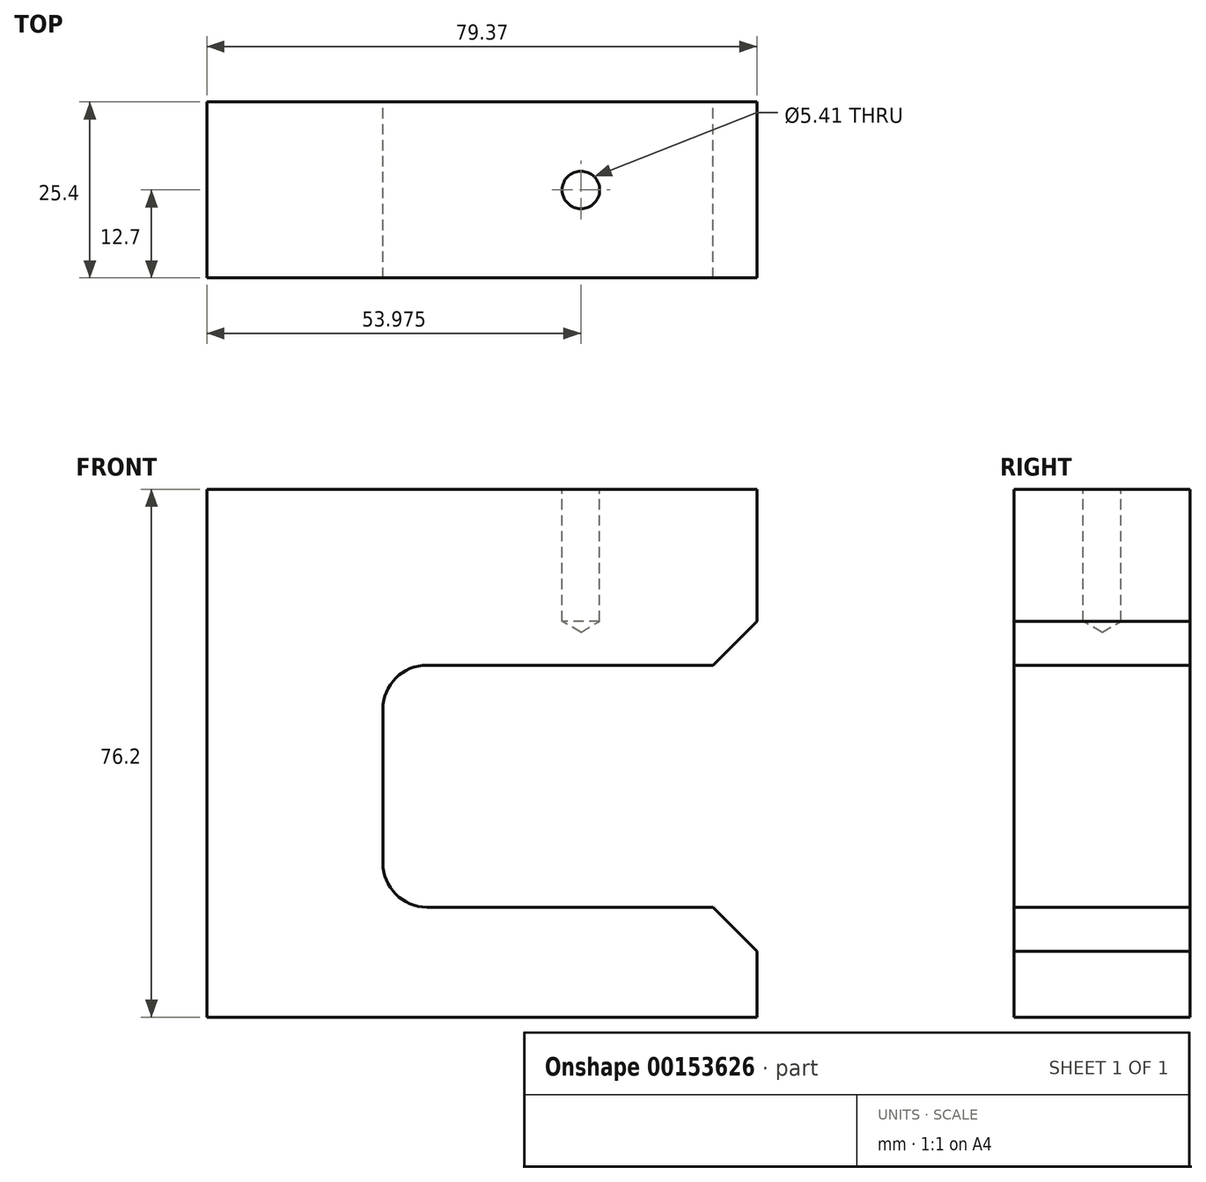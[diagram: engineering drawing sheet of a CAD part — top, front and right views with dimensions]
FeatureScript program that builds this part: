
annotation { "Feature Type Name" : "Feature", "Feature Type Description" : "" }
export const myFeature = defineFeature(function(context is Context, id is Id, definition is map)
    precondition{}
    {
        {
            var Q0;
            Q0=qCreatedBy(makeId("Front.planeOp"),FACE);
            var sketch = newSketch(context, id + "F0", { "sketchPlane" : qUnion([Q0])});
            skLineSegment(sketch, "E0", {"start": v(-38.1, 42.86) * mm, "end": v(-38.1, -33.34) * mm});
            skLineSegment(sketch, "E1", {"start": v(-38.1, -33.34) * mm, "end": v(41.28, -33.34) * mm});
            skLineSegment(sketch, "E2", {"start": v(41.28, -33.34) * mm, "end": v(41.28, -17.46) * mm});
            skLineSegment(sketch, "E3", {"start": v(41.28, -17.46) * mm, "end": v(-12.7, -17.46) * mm});
            skLineSegment(sketch, "E4", {"start": v(-12.7, -17.46) * mm, "end": v(-12.7, 17.46) * mm});
            skLineSegment(sketch, "E5", {"start": v(-12.7, 17.46) * mm, "end": v(41.28, 17.46) * mm});
            skLineSegment(sketch, "E6", {"start": v(41.28, 17.46) * mm, "end": v(41.28, 42.86) * mm});
            skLineSegment(sketch, "E7", {"start": v(41.28, 42.86) * mm, "end": v(-38.1, 42.86) * mm});
            skSolve(sketch);
        }
        {
            var Q0;
            Q0=makeQuery(id+"F0.imprint","IMPRINT",FACE,{"disambiguationData":[TD([[makeQuery(id+"F0.imprint","IMPRINT",EDGE,{"derivedFrom":sQuery(id+"F0.wireOp",EDGE,"E0")}),1.0]])]});
            extrude(context, id + "F1", {"entities" : qUnion([Q0]), "depth" : 25.4 * mm});
        }
        {
            var Q0;
            Q0=makeQuery(id+"F1.opExtrude","SWEPT_EDGE",EDGE,{"disambiguationData":[OSD([sQuery(id+"F0.wireOp",EDGE,"E4"),sQuery(id+"F0.wireOp",EDGE,"E5")])]});
            var Q1;
            Q1=makeQuery(id+"F1.opExtrude","SWEPT_EDGE",EDGE,{"disambiguationData":[OSD([sQuery(id+"F0.wireOp",EDGE,"E3"),sQuery(id+"F0.wireOp",EDGE,"E4")])]});
            fillet(context, id + "F2", {"entities" : qUnion([Q0, Q1]), "radius" : 6.35 * mm, "tangentPropagation" : true, "allowEdgeOverflow" : false});
        }
        {
            var Q0;
            Q0=makeQuery(id+"F1.opExtrude","SWEPT_EDGE",EDGE,{"disambiguationData":[OSD([sQuery(id+"F0.wireOp",EDGE,"E2"),sQuery(id+"F0.wireOp",EDGE,"E3")])]});
            var Q1;
            Q1=makeQuery(id+"F1.opExtrude","SWEPT_EDGE",EDGE,{"disambiguationData":[OSD([sQuery(id+"F0.wireOp",EDGE,"E5"),sQuery(id+"F0.wireOp",EDGE,"E6")])]});
            chamfer(context, id + "F3", {"entities" : qUnion([Q0, Q1]), "width" : 6.35 * mm, "tangentPropagation" : true});
        }
        {
            var Q0;
            Q0=makeQuery(id+"F1.opExtrude","SWEPT_FACE",FACE,{"disambiguationData":[OSD([sQuery(id+"F0.wireOp",EDGE,"E7")])]});
            var sketch = newSketch(context, id + "F4", { "sketchPlane" : qUnion([Q0])});
            skPoint(sketch, "E8", {"position": v(15.88, -12.7) * mm});
            skPoint(sketch, "E9", {"position": v(-19.05, -12.7) * mm});
            skSolve(sketch);
        }
        {
            var Q0;
            Q0=sQuery(id+"F4.wireOp",VERTEX,"E8");
            var Q1;
            Q1=makeQuery(id+"F1.opExtrude","SWEPT_BODY",BODY,{"disambiguationData":[OSD([sQuery(id+"F0.wireOp",EDGE,"E0"),sQuery(id+"F0.wireOp",EDGE,"E1"),sQuery(id+"F0.wireOp",EDGE,"E2"),sQuery(id+"F0.wireOp",EDGE,"E3"),sQuery(id+"F0.wireOp",EDGE,"E4"),sQuery(id+"F0.wireOp",EDGE,"E5"),sQuery(id+"F0.wireOp",EDGE,"E6"),sQuery(id+"F0.wireOp",EDGE,"E7")])]});
            hole(context, id + "F5", {"style" : HoleStyle.SIMPLE, "endStyle" : HoleEndStyle.BLIND, "standardTappedOrClearance" : lookupTablePath({ "standard" : "ANSI", "engagement" : "75%", "pitch" : "28 tpi", "size" : "1/4", "type" : "Tapped" }), "standardBlindInLast" : lookupTablePath({ "standard" : "ANSI", "engagement" : "75%", "pitch" : "28 tpi", "size" : "1/4", "type" : "Tapped" }), "holeDiameter" : 5.4 * mm, "holeDepth" : 19.05 * mm, "locations" : qUnion([Q0]), "scope" : qUnion([Q1]), "majorDiameter" : 6.35 * mm});
        }
    });
